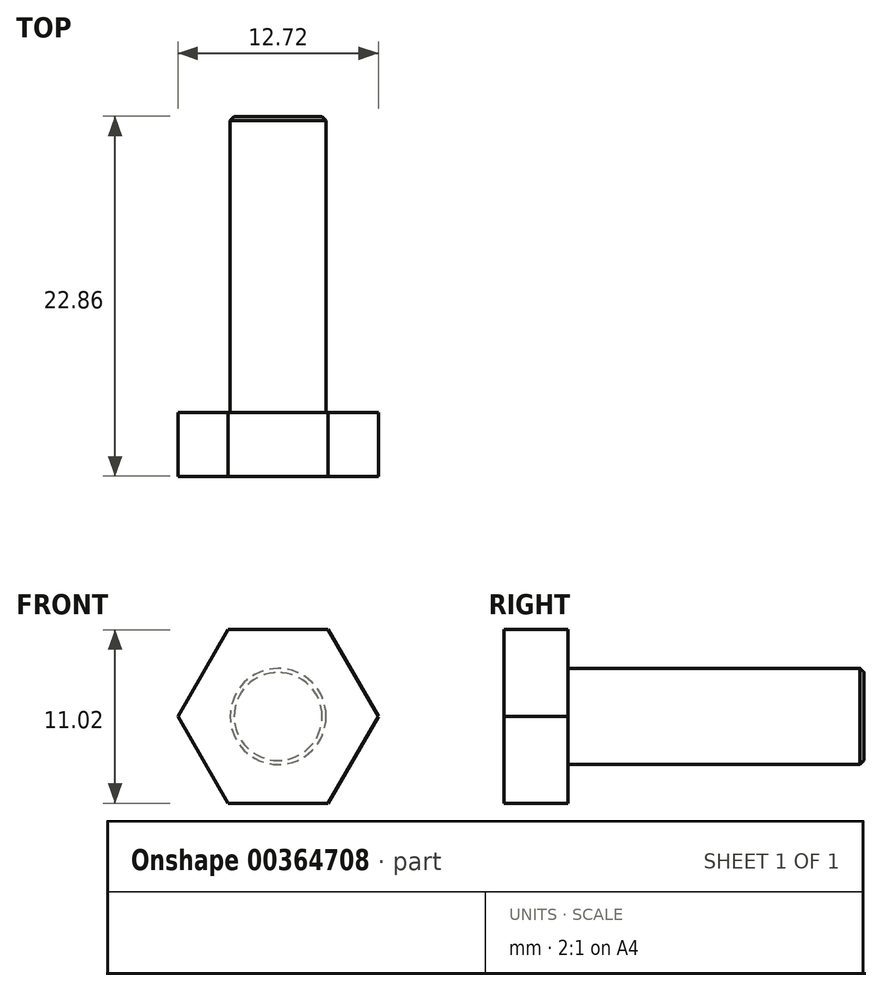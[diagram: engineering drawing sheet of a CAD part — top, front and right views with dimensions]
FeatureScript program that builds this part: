
annotation { "Feature Type Name" : "Feature", "Feature Type Description" : "" }
export const myFeature = defineFeature(function(context is Context, id is Id, definition is map)
    precondition{}
    {
        {
            var Q0;
            Q0=qCreatedBy(makeId("Front.planeOp"),FACE);
            var sketch = newSketch(context, id + "F0", { "sketchPlane" : qUnion([Q0])});
            skCircle(sketch, "E0.cCircle", {"center": v(0, 0) * mm, "radius": 5.51 * mm, "construction": true});
            skLineSegment(sketch, "E0.0", {"start": v(-3.18, 5.51) * mm, "end": v(3.18, 5.51) * mm});
            skLineSegment(sketch, "E0.1", {"start": v(3.18, 5.51) * mm, "end": v(6.36, 0) * mm});
            skLineSegment(sketch, "E0.2", {"start": v(6.36, 0) * mm, "end": v(3.18, -5.51) * mm});
            skLineSegment(sketch, "E0.3", {"start": v(3.18, -5.51) * mm, "end": v(-3.18, -5.51) * mm});
            skLineSegment(sketch, "E0.4", {"start": v(-3.18, -5.51) * mm, "end": v(-6.36, 0) * mm});
            skLineSegment(sketch, "E0.5", {"start": v(-6.36, 0) * mm, "end": v(-3.18, 5.51) * mm});
            skPoint(sketch, "E0.0.midPoint", {"position": v(0, 5.51) * mm});
            skSolve(sketch);
        }
        {
            var Q0;
            Q0 = qSketchRegion(id + "F0", true);
            extrude(context, id + "F1", {"entities" : qUnion([Q0]), "depth" : 4.06 * mm});
        }
        {
            var Q0;
            Q0=makeQuery(id+"F1.opExtrude","CAP_FACE",FACE,{"disambiguationData":[OSD([sQuery(id+"F0.wireOp",EDGE,"E0.0"),sQuery(id+"F0.wireOp",EDGE,"E0.1"),sQuery(id+"F0.wireOp",EDGE,"E0.2"),sQuery(id+"F0.wireOp",EDGE,"E0.3"),sQuery(id+"F0.wireOp",EDGE,"E0.4"),sQuery(id+"F0.wireOp",EDGE,"E0.5")])],"isStart":true});
            var sketch = newSketch(context, id + "F2", { "sketchPlane" : qUnion([Q0])});
            skCircle(sketch, "E1", {"center": v(0, 0) * mm, "radius": 3.05 * mm});
            skSolve(sketch);
        }
        {
            var Q0;
            Q0 = qSketchRegion(id + "F2", true);
            extrude(context, id + "F3", {"entities" : qUnion([Q0]), "operationType" : NewBodyOperationType.ADD, "depth" : 18.8 * mm});
        }
        {
            var Q0;
            Q0=makeQuery(id+"F3.opExtrude","CAP_EDGE",EDGE,{"disambiguationData":[OSD([sQuery(id+"F2.wireOp",EDGE,"E1")])],"isStart":false});
            chamfer(context, id + "F4", {"entities" : qUnion([Q0]), "width" : 0.25 * mm, "tangentPropagation" : true});
        }
    });
